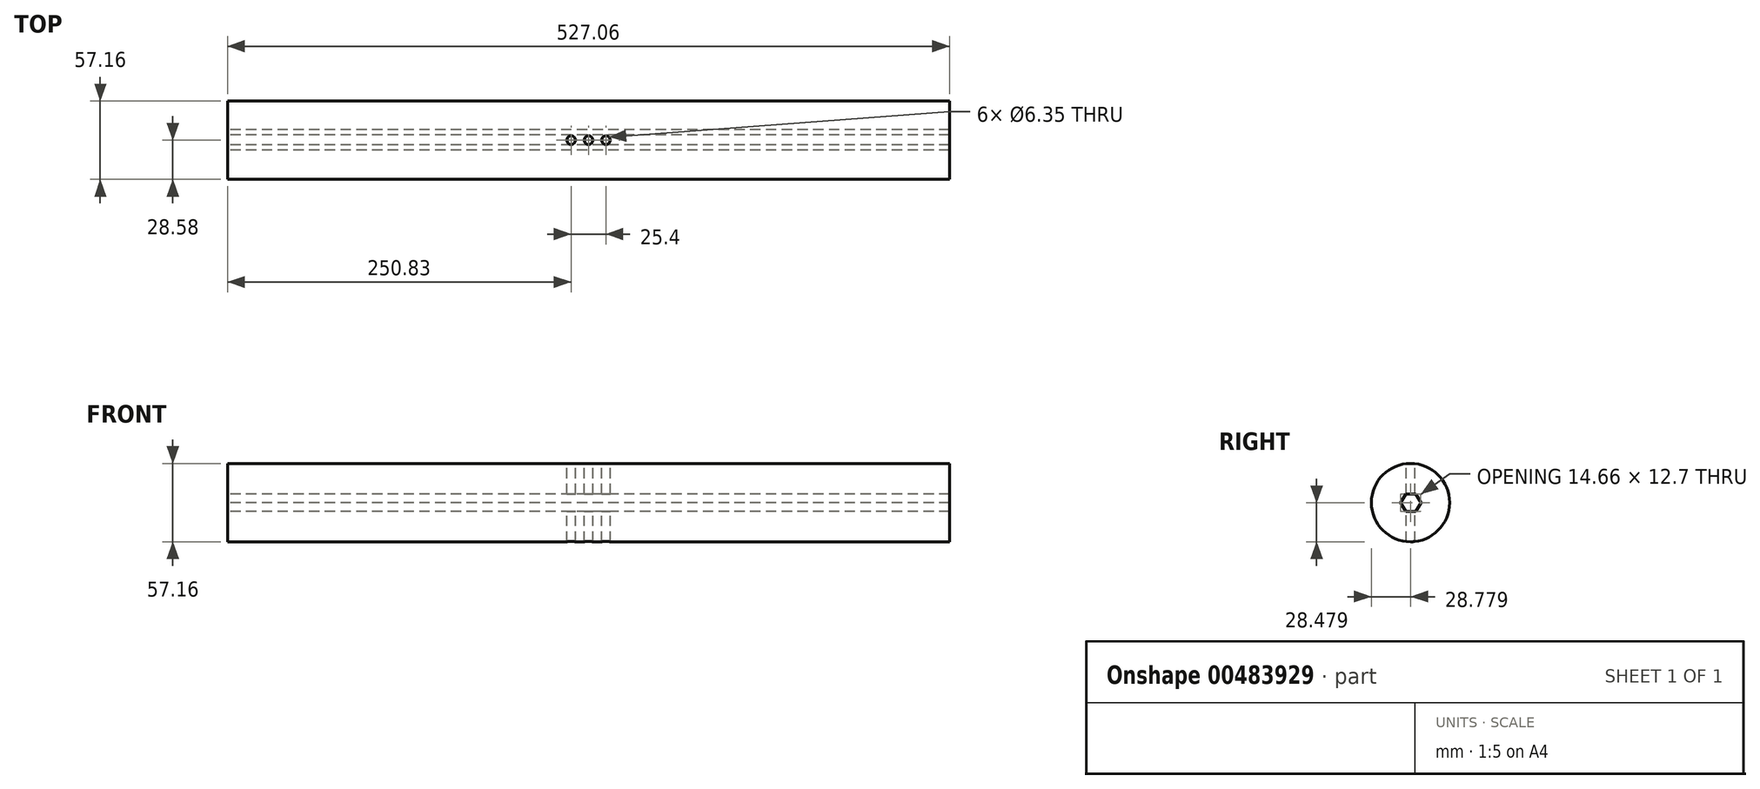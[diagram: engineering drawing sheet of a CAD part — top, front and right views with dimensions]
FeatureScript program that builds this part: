
annotation { "Feature Type Name" : "Feature", "Feature Type Description" : "" }
export const myFeature = defineFeature(function(context is Context, id is Id, definition is map)
    precondition{}
    {
        {
            var Q0;
            Q0=qCreatedBy(makeId("Right.planeOp"),FACE);
            var sketch = newSketch(context, id + "F0", { "sketchPlane" : qUnion([Q0])});
            skCircle(sketch, "E0", {"center": v(0, 0) * mm, "radius": 28.58 * mm});
            skLineSegment(sketch, "E1.0", {"start": v(3.86, 6.25) * mm, "end": v(7.53, -0.1) * mm});
            skLineSegment(sketch, "E1.1", {"start": v(7.53, -0.1) * mm, "end": v(3.86, -6.45) * mm});
            skLineSegment(sketch, "E1.2", {"start": v(3.86, -6.45) * mm, "end": v(-3.47, -6.45) * mm});
            skLineSegment(sketch, "E1.3", {"start": v(-3.47, -6.45) * mm, "end": v(-7.13, -0.1) * mm});
            skLineSegment(sketch, "E1.4", {"start": v(-7.13, -0.1) * mm, "end": v(-3.47, 6.25) * mm});
            skLineSegment(sketch, "E1.5", {"start": v(-3.47, 6.25) * mm, "end": v(3.86, 6.25) * mm});
            skSolve(sketch);
        }
        {
            var Q0;
            Q0 = qSketchRegion(id + "F0", true);
            extrude(context, id + "F1", {"entities" : qUnion([Q0]), "endBound" : BoundingType.SYMMETRIC, "depth" : 527.05 * mm, "offsetDistance" : 25.4 * mm});
        }
        {
            var Q0;
            Q0=qCreatedBy(makeId("Top.planeOp"),FACE);
            cPlane(context, id + "F2", {"entities" : qUnion([Q0]), "cplaneType" : CPlaneType.OFFSET, "offset" : 28.57 * mm, "width" : 152.4 * mm, "height" : 152.4 * mm});
        }
        {
            var Q0;
            Q0=qCreatedBy(id+"F2.planeOp",FACE);
            var sketch = newSketch(context, id + "F3", { "sketchPlane" : qUnion([Q0])});
            skCircle(sketch, "E2", {"center": v(0, 0) * mm, "radius": 3.18 * mm});
            skCircle(sketch, "E3", {"center": v(-12.7, 0) * mm, "radius": 3.18 * mm});
            skCircle(sketch, "E4", {"center": v(12.7, 0) * mm, "radius": 3.18 * mm});
            skSolve(sketch);
        }
        {
            var Q0;
            Q0 = qSketchRegion(id + "F3", true);
            extrude(context, id + "F4", {"entities" : qUnion([Q0]), "operationType" : NewBodyOperationType.REMOVE, "oppositeDirection" : true, "depth" : 91.7 * mm});
        }
    });
